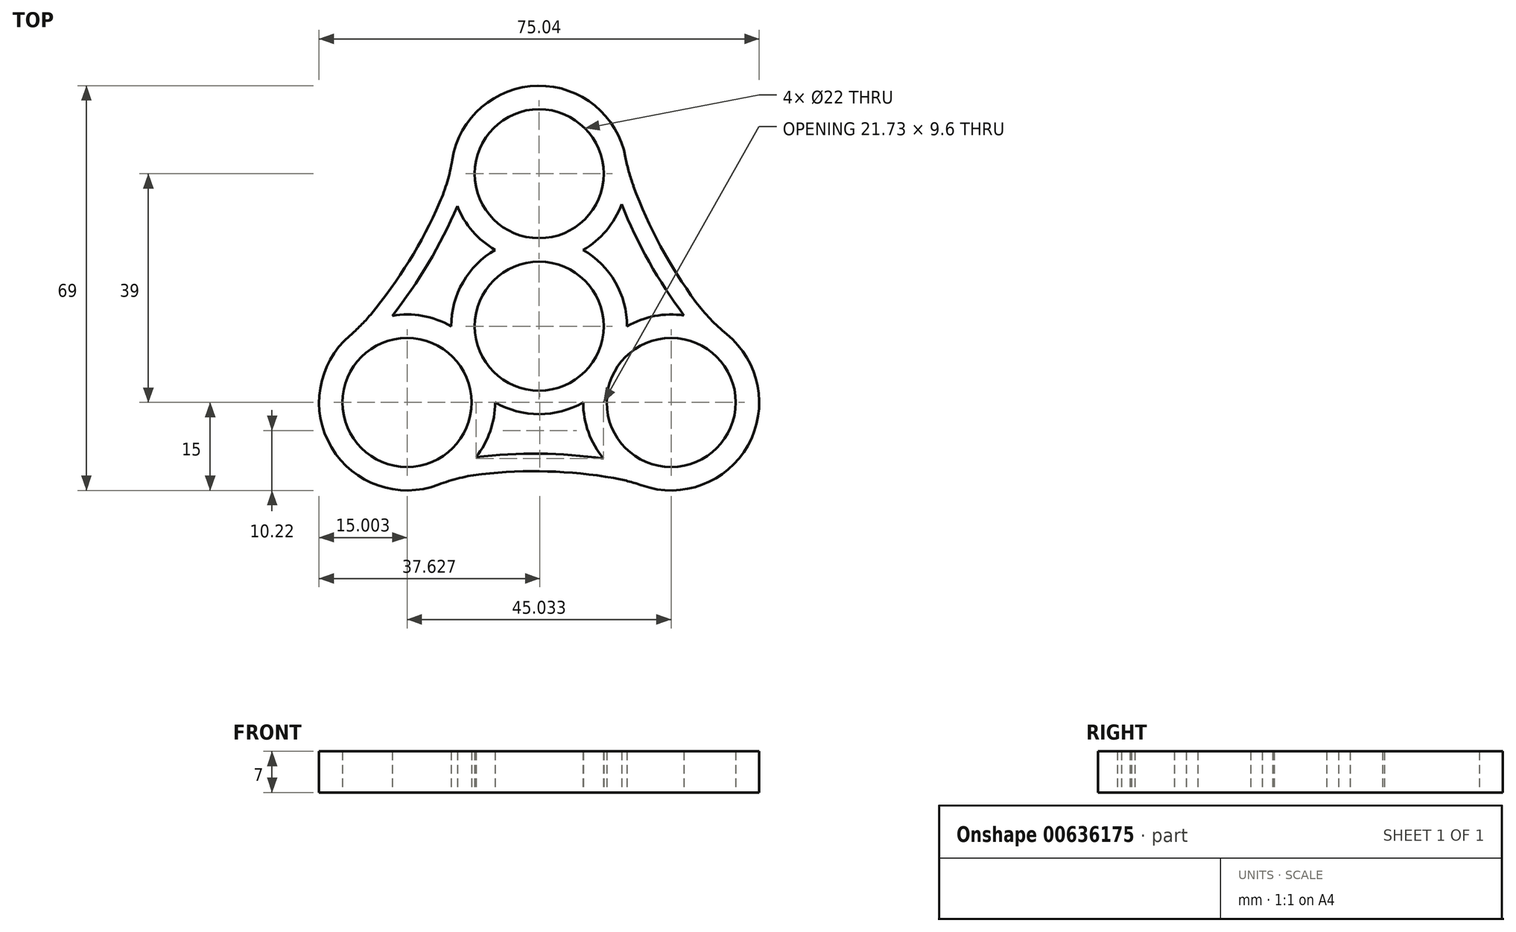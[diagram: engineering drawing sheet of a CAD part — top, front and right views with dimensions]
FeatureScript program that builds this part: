
annotation { "Feature Type Name" : "Feature", "Feature Type Description" : "" }
export const myFeature = defineFeature(function(context is Context, id is Id, definition is map)
    precondition{}
    {
        {
            var Q0;
            Q0=qCreatedBy(makeId("Top.planeOp"),FACE);
            var sketch = newSketch(context, id + "F0", { "sketchPlane" : qUnion([Q0])});
            skCircle(sketch, "E0", {"center": v(0, 0) * mm, "radius": 11 * mm});
            skCircle(sketch, "E1", {"center": v(0, 0) * mm, "radius": 15 * mm});
            skCircle(sketch, "E2", {"center": v(0, 0) * mm, "radius": 26 * mm, "construction": true});
            skCircle(sketch, "E3", {"center": v(0, 26) * mm, "radius": 11 * mm});
            skCircle(sketch, "E4", {"center": v(0, 26) * mm, "radius": 15 * mm});
            skCircle(sketch, "E5.1.0", {"center": v(-22.52, -13) * mm, "radius": 15 * mm});
            skCircle(sketch, "E5.1.1", {"center": v(-22.52, -13) * mm, "radius": 11 * mm});
            skCircle(sketch, "E5.2.0", {"center": v(22.52, -13) * mm, "radius": 15 * mm});
            skCircle(sketch, "E5.2.1", {"center": v(22.52, -13) * mm, "radius": 11 * mm});
            skArc(sketch, "E6", {"start": v(14.95, 27.2) * mm, "mid": v(21.14, 12.86) * mm, "end": v(30, 0) * mm});
            skArc(sketch, "E7.0", {"start": v(14.07, 20.8) * mm, "mid": v(18.76, 10.97) * mm, "end": v(24.7, 1.84) * mm});
            skArc(sketch, "E8.1.0", {"start": v(-31.03, -0.65) * mm, "mid": v(-21.7, 11.88) * mm, "end": v(-15, 25.98) * mm});
            skArc(sketch, "E8.1.1", {"start": v(-25.04, 1.79) * mm, "mid": v(-18.88, 10.77) * mm, "end": v(-13.95, 20.48) * mm});
            skArc(sketch, "E8.2.0", {"start": v(16.07, -26.55) * mm, "mid": v(0.56, -24.74) * mm, "end": v(-15, -25.98) * mm});
            skArc(sketch, "E8.2.1", {"start": v(10.97, -22.58) * mm, "mid": v(0.12, -21.73) * mm, "end": v(-10.76, -22.32) * mm});
            skSolve(sketch);
        }
        {
            var Q0;
            {var subQ0=sQuery(id+"F0.wireOp",EDGE,"E3");Q0=makeQuery(id+"F0.imprint","IMPRINT",FACE,{"disambiguationData":[TD([[makeQuery(id+"F0.imprint","IMPRINT",EDGE,{"derivedFrom":subQ0}),-1.0]])]});}
            var Q1;
            {var subQ0=sQuery(id+"F0.wireOp",EDGE,"E1");var subQ1=makeQuery(id+"F0.imprint","INTERSECT",VERTEX,{"derivedFrom":[subQ0,sQuery(id+"F0.wireOp",EDGE,"E3")]});Q1=makeQuery(id+"F0.imprint","IMPRINT",FACE,{"disambiguationData":[TD([[makeQuery(id+"F0.imprint","IMPRINT",EDGE,{"disambiguationData":[TD([[subQ1,1.0]])],"derivedFrom":subQ0}),1.0]])]});}
            var Q2;
            {var subQ0=sQuery(id+"F0.wireOp",EDGE,"E4");var subQ1=sQuery(id+"F0.wireOp",EDGE,"E0");var subQ2=makeQuery(id+"F0.imprint","INTERSECT",VERTEX,{"derivedFrom":[subQ1,subQ0]});Q2=makeQuery(id+"F0.imprint","IMPRINT",FACE,{"disambiguationData":[TD([[makeQuery(id+"F0.imprint","IMPRINT",EDGE,{"disambiguationData":[TD([[subQ2,1.0]])],"derivedFrom":subQ1}),-1.0]])]});}
            var Q3;
            {var subQ0=sQuery(id+"F0.wireOp",EDGE,"E6");Q3=makeQuery(id+"F0.imprint","IMPRINT",FACE,{"disambiguationData":[TD([[makeQuery(id+"F0.imprint","IMPRINT",EDGE,{"derivedFrom":subQ0}),-1.0]])]});}
            var Q4;
            {var subQ3=sQuery(id+"F0.wireOp",EDGE,"E5.2.1");Q4=makeQuery(id+"F0.imprint","IMPRINT",FACE,{"disambiguationData":[TD([[makeQuery(id+"F0.imprint","IMPRINT",EDGE,{"derivedFrom":subQ3}),-1.0]])]});}
            var Q5;
            {var subQ0=sQuery(id+"F0.wireOp",EDGE,"E1");var subQ1=makeQuery(id+"F0.imprint","INTERSECT",VERTEX,{"derivedFrom":[subQ0,sQuery(id+"F0.wireOp",EDGE,"E5.2.1")]});Q5=makeQuery(id+"F0.imprint","IMPRINT",FACE,{"disambiguationData":[TD([[makeQuery(id+"F0.imprint","IMPRINT",EDGE,{"disambiguationData":[TD([[subQ1,1.0]])],"derivedFrom":subQ0}),1.0]])]});}
            var Q6;
            {var subQ0=sQuery(id+"F0.wireOp",EDGE,"E5.1.0");var subQ1=sQuery(id+"F0.wireOp",EDGE,"E0");var subQ2=makeQuery(id+"F0.imprint","INTERSECT",VERTEX,{"derivedFrom":[subQ1,subQ0]});Q6=makeQuery(id+"F0.imprint","IMPRINT",FACE,{"disambiguationData":[TD([[makeQuery(id+"F0.imprint","IMPRINT",EDGE,{"disambiguationData":[TD([[subQ2,-1.0]])],"derivedFrom":subQ1}),-1.0]])]});}
            var Q7;
            {var subQ0=sQuery(id+"F0.wireOp",EDGE,"E8.2.0");Q7=makeQuery(id+"F0.imprint","IMPRINT",FACE,{"disambiguationData":[TD([[makeQuery(id+"F0.imprint","IMPRINT",EDGE,{"derivedFrom":subQ0}),-1.0]])]});}
            var Q8;
            {var subQ3=sQuery(id+"F0.wireOp",EDGE,"E5.1.1");Q8=makeQuery(id+"F0.imprint","IMPRINT",FACE,{"disambiguationData":[TD([[makeQuery(id+"F0.imprint","IMPRINT",EDGE,{"derivedFrom":subQ3}),-1.0]])]});}
            var Q9;
            {var subQ0=sQuery(id+"F0.wireOp",EDGE,"E1");var subQ1=makeQuery(id+"F0.imprint","INTERSECT",VERTEX,{"derivedFrom":[subQ0,sQuery(id+"F0.wireOp",EDGE,"E5.1.1")]});Q9=makeQuery(id+"F0.imprint","IMPRINT",FACE,{"disambiguationData":[TD([[makeQuery(id+"F0.imprint","IMPRINT",EDGE,{"disambiguationData":[TD([[subQ1,1.0]])],"derivedFrom":subQ0}),1.0]])]});}
            var Q10;
            {var subQ0=sQuery(id+"F0.wireOp",EDGE,"E5.1.0");var subQ1=sQuery(id+"F0.wireOp",EDGE,"E0");var subQ2=makeQuery(id+"F0.imprint","INTERSECT",VERTEX,{"derivedFrom":[subQ1,subQ0]});Q10=makeQuery(id+"F0.imprint","IMPRINT",FACE,{"disambiguationData":[TD([[makeQuery(id+"F0.imprint","IMPRINT",EDGE,{"disambiguationData":[TD([[subQ2,1.0]])],"derivedFrom":subQ1}),-1.0]])]});}
            var Q11;
            {var subQ0=sQuery(id+"F0.wireOp",EDGE,"E8.1.0");Q11=makeQuery(id+"F0.imprint","IMPRINT",FACE,{"disambiguationData":[TD([[makeQuery(id+"F0.imprint","IMPRINT",EDGE,{"derivedFrom":subQ0}),-1.0]])]});}
            extrude(context, id + "F1", {"entities" : qUnion([Q0, Q1, Q2, Q3, Q4, Q5, Q6, Q7, Q8, Q9, Q10, Q11]), "depth" : 7 * mm, "offsetDistance" : 25 * mm});
        }
        {
            var Q0;
            Q0=makeQuery(id+"F1.opExtrude","SWEPT_EDGE",EDGE,{"disambiguationData":[OSD([sQuery(id+"F0.wireOp",EDGE,"E4"),sQuery(id+"F0.wireOp",EDGE,"E8.1.0")])]});
            var Q1;
            Q1=makeQuery(id+"F1.opExtrude","SWEPT_EDGE",EDGE,{"disambiguationData":[OSD([sQuery(id+"F0.wireOp",EDGE,"E5.1.0"),sQuery(id+"F0.wireOp",EDGE,"E8.1.0")])]});
            var Q2;
            Q2=makeQuery(id+"F1.opExtrude","SWEPT_EDGE",EDGE,{"disambiguationData":[OSD([sQuery(id+"F0.wireOp",EDGE,"E5.1.0"),sQuery(id+"F0.wireOp",EDGE,"E8.2.0")])]});
            var Q3;
            Q3=makeQuery(id+"F1.opExtrude","SWEPT_EDGE",EDGE,{"disambiguationData":[OSD([sQuery(id+"F0.wireOp",EDGE,"E5.2.0"),sQuery(id+"F0.wireOp",EDGE,"E8.2.0")])]});
            var Q4;
            Q4=makeQuery(id+"F1.opExtrude","SWEPT_EDGE",EDGE,{"disambiguationData":[OSD([sQuery(id+"F0.wireOp",EDGE,"E4"),sQuery(id+"F0.wireOp",EDGE,"E6")])]});
            var Q5;
            Q5=makeQuery(id+"F1.opExtrude","SWEPT_EDGE",EDGE,{"disambiguationData":[OSD([sQuery(id+"F0.wireOp",EDGE,"E5.2.0"),sQuery(id+"F0.wireOp",EDGE,"E6")])]});
            fillet(context, id + "F2", {"entities" : qUnion([Q0, Q1, Q2, Q3, Q4, Q5]), "radius" : 30 * mm, "tangentPropagation" : true, "allowEdgeOverflow" : false});
        }
    });
